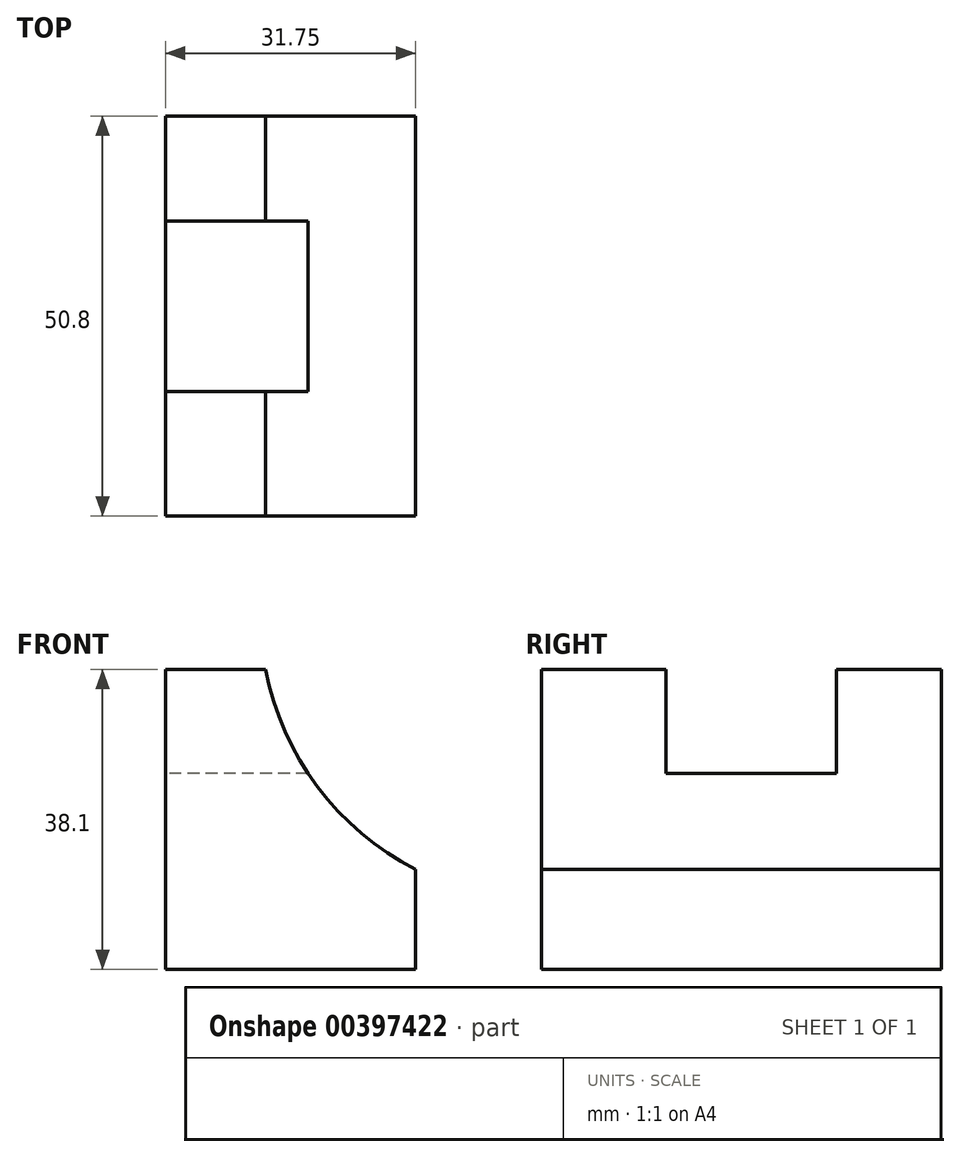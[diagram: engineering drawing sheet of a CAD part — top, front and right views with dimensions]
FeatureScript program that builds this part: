
annotation { "Feature Type Name" : "Feature", "Feature Type Description" : "" }
export const myFeature = defineFeature(function(context is Context, id is Id, definition is map)
    precondition{}
    {
        {
            var Q0;
            Q0=qCreatedBy(makeId("Front.planeOp"),FACE);
            var sketch = newSketch(context, id + "F0", { "sketchPlane" : qUnion([Q0])});
            skLineSegment(sketch, "E0", {"start": v(0, 38.1) * mm, "end": v(0, 0) * mm});
            skLineSegment(sketch, "E1", {"start": v(0, 0) * mm, "end": v(31.75, 0) * mm});
            skLineSegment(sketch, "E2", {"start": v(31.75, 0) * mm, "end": v(31.75, 12.7) * mm});
            skLineSegment(sketch, "E3", {"start": v(0, 38.1) * mm, "end": v(12.7, 38.1) * mm});
            skArc(sketch, "E4", {"start": v(12.7, 38.1) * mm, "mid": v(19.3, 23.2) * mm, "end": v(31.75, 12.7) * mm});
            skSolve(sketch);
        }
        {
            var Q0;
            Q0 = qSketchRegion(id + "F0", true);
            extrude(context, id + "F1", {"entities" : qUnion([Q0]), "depth" : 50.8 * mm});
        }
        {
            var Q0;
            Q0=qCreatedBy(makeId("Right.planeOp"),FACE);
            var sketch = newSketch(context, id + "F2", { "sketchPlane" : qUnion([Q0])});
            skLineSegment(sketch, "E5", {"start": v(-37.45, 38.16) * mm, "end": v(-37.45, 22.5) * mm});
            skLineSegment(sketch, "E6", {"start": v(-37.45, 22.5) * mm, "end": v(-12.05, 22.5) * mm});
            skLineSegment(sketch, "E7", {"start": v(-37.45, 38.16) * mm, "end": v(-12.05, 38.16) * mm});
            skLineSegment(sketch, "E8", {"start": v(-12.05, 38.16) * mm, "end": v(-37.45, 38.16) * mm});
            skLineSegment(sketch, "E9", {"start": v(-12.05, 38.16) * mm, "end": v(-12.05, 22.5) * mm});
            skSolve(sketch);
        }
        {
            var Q0;
            Q0 = qSketchRegion(id + "F2", true);
            extrude(context, id + "F3", {"entities" : qUnion([Q0]), "operationType" : NewBodyOperationType.REMOVE, "oppositeDirection" : true, "depth" : 50.8 * mm});
        }
        {
            var Q0;
            Q0=qCreatedBy(makeId("Right.planeOp"),FACE);
            var sketch = newSketch(context, id + "F4", { "sketchPlane" : qUnion([Q0])});
            skLineSegment(sketch, "E10", {"start": v(-34.98, 38.53) * mm, "end": v(-34.98, 24.92) * mm});
            skLineSegment(sketch, "E11", {"start": v(-34.98, 24.92) * mm, "end": v(-13.3, 24.92) * mm});
            skLineSegment(sketch, "E12", {"start": v(-13.3, 24.92) * mm, "end": v(-13.3, 38.53) * mm});
            skLineSegment(sketch, "E13", {"start": v(-13.3, 38.53) * mm, "end": v(-34.98, 38.53) * mm});
            skSolve(sketch);
        }
        {
            var Q0;
            Q0 = qSketchRegion(id + "F4", true);
            extrude(context, id + "F5", {"entities" : qUnion([Q0]), "operationType" : NewBodyOperationType.REMOVE, "depth" : 85.34 * mm});
        }
    });
